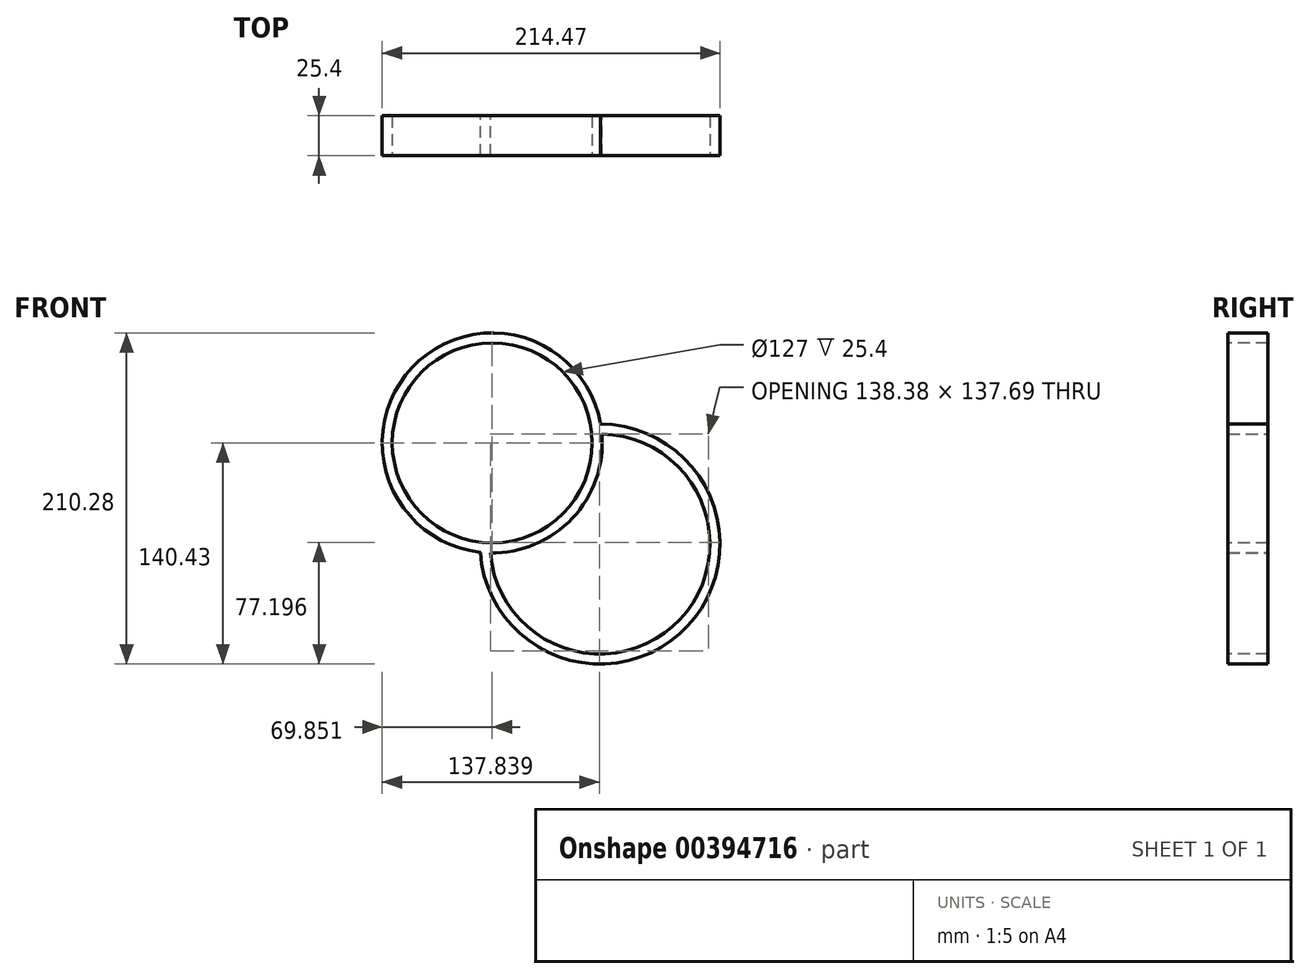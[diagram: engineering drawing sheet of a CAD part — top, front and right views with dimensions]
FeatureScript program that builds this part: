
annotation { "Feature Type Name" : "Feature", "Feature Type Description" : "" }
export const myFeature = defineFeature(function(context is Context, id is Id, definition is map)
    precondition{}
    {
        {
            var Q0;
            Q0=qCreatedBy(makeId("Front.planeOp"),FACE);
            var sketch = newSketch(context, id + "F0", { "sketchPlane" : qUnion([Q0])});
            skCircle(sketch, "E0", {"center": v(-6.1, 2.88) * mm, "radius": 76.2 * mm});
            skSolve(sketch);
        }
        {
            var Q0;
            Q0=makeQuery(id+"F0.imprint","IMPRINT",FACE,{"disambiguationData":[TD([[makeQuery(id+"F0.imprint","IMPRINT",EDGE,{"derivedFrom":sQuery(id+"F0.wireOp",EDGE,"E0")}),1.0]])]});
            extrude(context, id + "F1", {"entities" : qUnion([Q0]), "depth" : 25.4 * mm});
        }
        {
            var Q0;
            Q0=makeQuery(id+"F1.opExtrude","CAP_FACE",FACE,{"disambiguationData":[OSD([sQuery(id+"F0.wireOp",EDGE,"E0")])],"isStart":false});
            var sketch = newSketch(context, id + "F2", { "sketchPlane" : qUnion([Q0])});
            skPoint(sketch, "E1", {"position": v(-6.1, 2.88) * mm});
            skSolve(sketch);
        }
        {
            var Q0;
            Q0=sQuery(id+"F2.wireOp",VERTEX,"E1");
            var Q1;
            Q1=makeQuery(id+"F1.opExtrude","SWEPT_BODY",BODY,{"disambiguationData":[OSD([sQuery(id+"F0.wireOp",EDGE,"E0")])]});
            hole(context, id + "F3", {"style" : HoleStyle.SIMPLE, "endStyle" : HoleEndStyle.THROUGH, "holeDiameter" : 139.7 * mm, "isTappedThrough" : true, "tappedDepth" : 12.7 * mm, "tapClearance" : 3, "locations" : qUnion([Q0]), "scope" : qUnion([Q1])});
        }
        {
            var Q0;
            Q0=qCreatedBy(makeId("Front.planeOp"),FACE);
            var sketch = newSketch(context, id + "F4", { "sketchPlane" : qUnion([Q0])});
            skCircle(sketch, "E2", {"center": v(-74.53, 67.11) * mm, "radius": 69.85 * mm});
            skSolve(sketch);
        }
        {
            var Q0;
            Q0=makeQuery(id+"F4.imprint","IMPRINT",FACE,{"disambiguationData":[TD([[makeQuery(id+"F4.imprint","IMPRINT",EDGE,{"derivedFrom":sQuery(id+"F4.wireOp",EDGE,"E2")}),1.0]])]});
            extrude(context, id + "F5", {"entities" : qUnion([Q0]), "operationType" : NewBodyOperationType.ADD, "depth" : 25.4 * mm});
        }
        {
            var Q0;
            Q0=makeQuery(id+"F5.boolean.opBoolean","MERGE",FACE,{"derivedFrom":[makeQuery(id+"F1.opExtrude","CAP_FACE",FACE,{"disambiguationData":[OSD([sQuery(id+"F0.wireOp",EDGE,"E0")])],"isStart":false}),makeQuery(id+"F5.opExtrude","CAP_FACE",FACE,{"disambiguationData":[OSD([sQuery(id+"F4.wireOp",EDGE,"E2")])],"isStart":false})]});
            var sketch = newSketch(context, id + "F6", { "sketchPlane" : qUnion([Q0])});
            skPoint(sketch, "E3", {"position": v(-74.53, 67.11) * mm});
            skSolve(sketch);
        }
        {
            var Q0;
            Q0=sQuery(id+"F6.wireOp",VERTEX,"E3");
            var Q1;
            Q1=makeQuery(id+"F1.opExtrude","SWEPT_BODY",BODY,{"disambiguationData":[OSD([sQuery(id+"F0.wireOp",EDGE,"E0")])]});
            hole(context, id + "F7", {"style" : HoleStyle.SIMPLE, "endStyle" : HoleEndStyle.THROUGH, "holeDiameter" : 127 * mm, "isTappedThrough" : true, "tappedDepth" : 12.7 * mm, "tapClearance" : 3, "locations" : qUnion([Q0]), "scope" : qUnion([Q1])});
        }
    });
